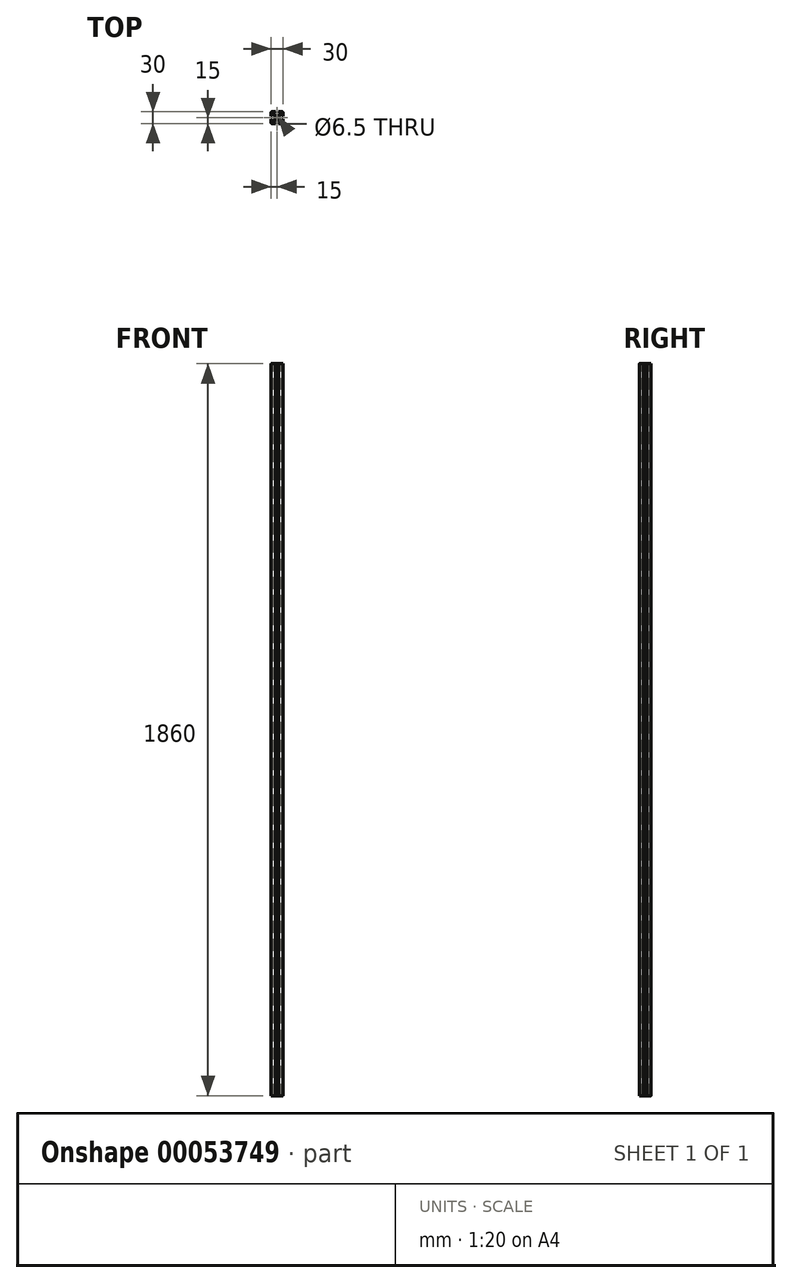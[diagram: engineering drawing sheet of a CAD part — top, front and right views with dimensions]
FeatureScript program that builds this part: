
annotation { "Feature Type Name" : "Feature", "Feature Type Description" : "" }
export const myFeature = defineFeature(function(context is Context, id is Id, definition is map)
    precondition{}
    {
        {
            var Q0;
            Q0=qCreatedBy(makeId("Top.planeOp"),FACE);
            var sketch = newSketch(context, id + "F0", { "sketchPlane" : qUnion([Q0])});
            skLineSegment(sketch, "E0.bottom", {"start": v(-15, 15) * mm, "end": v(15, 15) * mm});
            skLineSegment(sketch, "E0.top", {"start": v(-15, -15) * mm, "end": v(15, -15) * mm});
            skLineSegment(sketch, "E0.left", {"start": v(-15, 15) * mm, "end": v(-15, -15) * mm});
            skLineSegment(sketch, "E0.right", {"start": v(15, 15) * mm, "end": v(15, -15) * mm});
            skSolve(sketch);
        }
        {
            var Q0;
            Q0=qSketchRegion(id+"F0",true);
            extrude(context, id + "F1", {"entities" : qUnion([Q0]), "endBound" : BoundingType.SYMMETRIC, "depth" : (1900 - 40) * mm});
        }
        {
            var Q0;
            Q0=makeQuery(id+"F1.opExtrude","SWEPT_EDGE",EDGE,{"disambiguationData":[OSD([sQuery(id+"F0.wireOp",EDGE,"E0.bottom"),sQuery(id+"F0.wireOp",EDGE,"E0.right")])]});
            var Q1;
            Q1=makeQuery(id+"F1.opExtrude","SWEPT_EDGE",EDGE,{"disambiguationData":[OSD([sQuery(id+"F0.wireOp",EDGE,"E0.bottom"),sQuery(id+"F0.wireOp",EDGE,"E0.left")])]});
            var Q2;
            Q2=makeQuery(id+"F1.opExtrude","SWEPT_EDGE",EDGE,{"disambiguationData":[OSD([sQuery(id+"F0.wireOp",EDGE,"E0.top"),sQuery(id+"F0.wireOp",EDGE,"E0.right")])]});
            var Q3;
            Q3=makeQuery(id+"F1.opExtrude","SWEPT_EDGE",EDGE,{"disambiguationData":[OSD([sQuery(id+"F0.wireOp",EDGE,"E0.top"),sQuery(id+"F0.wireOp",EDGE,"E0.left")])]});
            fillet(context, id + "F2", {"entities" : qUnion([Q0, Q1, Q2, Q3]), "radius" : 2 * mm, "tangentPropagation" : true, "allowEdgeOverflow" : false});
        }
        {
            var Q0;
            Q0=makeQuery(id+"F1.opExtrude","CAP_FACE",FACE,{"disambiguationData":[OSD([sQuery(id+"F0.wireOp",EDGE,"E0.bottom"),sQuery(id+"F0.wireOp",EDGE,"E0.top"),sQuery(id+"F0.wireOp",EDGE,"E0.left"),sQuery(id+"F0.wireOp",EDGE,"E0.right")])],"isStart":false});
            var sketch = newSketch(context, id + "F3", { "sketchPlane" : qUnion([Q0])});
            skCircle(sketch, "E1", {"center": v(0, 0) * mm, "radius": 3.25 * mm});
            skSolve(sketch);
        }
        {
            var Q0;
            Q0=qSketchRegion(id+"F3",true);
            extrude(context, id + "F4", {"entities" : qUnion([Q0]), "operationType" : NewBodyOperationType.REMOVE, "endBound" : BoundingType.THROUGH_ALL, "oppositeDirection" : true, "depth" : 25 * mm});
        }
        {
            var Q0;
            Q0=makeQuery(id+"F1.opExtrude","CAP_FACE",FACE,{"disambiguationData":[OSD([sQuery(id+"F0.wireOp",EDGE,"E0.bottom"),sQuery(id+"F0.wireOp",EDGE,"E0.top"),sQuery(id+"F0.wireOp",EDGE,"E0.left"),sQuery(id+"F0.wireOp",EDGE,"E0.right")])],"isStart":false});
            var sketch = newSketch(context, id + "F5", { "sketchPlane" : qUnion([Q0])});
            skLineSegment(sketch, "E2", {"start": v(-4.2, 15) * mm, "end": v(4.2, 15) * mm});
            skLineSegment(sketch, "E3", {"start": v(4.2, 15) * mm, "end": v(4.2, 13) * mm});
            skLineSegment(sketch, "E4", {"start": v(4.2, 13) * mm, "end": v(8.25, 13) * mm});
            skLineSegment(sketch, "E5", {"start": v(8.25, 13) * mm, "end": v(8.25, 10) * mm});
            skLineSegment(sketch, "E6", {"start": v(8.25, 10) * mm, "end": v(3.85, 5.6) * mm});
            skLineSegment(sketch, "E7", {"start": v(3.85, 5.6) * mm, "end": v(-3.85, 5.6) * mm});
            skLineSegment(sketch, "E8", {"start": v(-3.85, 5.6) * mm, "end": v(-8.25, 10) * mm});
            skLineSegment(sketch, "E9", {"start": v(-4.2, 15) * mm, "end": v(-4.2, 13) * mm});
            skLineSegment(sketch, "E10", {"start": v(-4.2, 13) * mm, "end": v(-8.25, 13) * mm});
            skLineSegment(sketch, "E11", {"start": v(-8.25, 13) * mm, "end": v(-8.25, 10) * mm});
            skLineSegment(sketch, "E12.1.0", {"start": v(-15, -4.2) * mm, "end": v(-15, 4.2) * mm});
            skLineSegment(sketch, "E12.1.1", {"start": v(-15, 4.2) * mm, "end": v(-13, 4.2) * mm});
            skLineSegment(sketch, "E12.1.2", {"start": v(-13, 4.2) * mm, "end": v(-13, 8.25) * mm});
            skLineSegment(sketch, "E12.1.3", {"start": v(-13, 8.25) * mm, "end": v(-10, 8.25) * mm});
            skLineSegment(sketch, "E12.1.4", {"start": v(-10, 8.25) * mm, "end": v(-5.6, 3.85) * mm});
            skLineSegment(sketch, "E12.1.5", {"start": v(-5.6, 3.85) * mm, "end": v(-5.6, -3.85) * mm});
            skLineSegment(sketch, "E12.1.6", {"start": v(-5.6, -3.85) * mm, "end": v(-10, -8.25) * mm});
            skLineSegment(sketch, "E12.1.7", {"start": v(-13, -8.25) * mm, "end": v(-10, -8.25) * mm});
            skLineSegment(sketch, "E12.1.8", {"start": v(-13, -4.2) * mm, "end": v(-13, -8.25) * mm});
            skLineSegment(sketch, "E12.1.9", {"start": v(-15, -4.2) * mm, "end": v(-13, -4.2) * mm});
            skLineSegment(sketch, "E12.2.0", {"start": v(4.2, -15) * mm, "end": v(-4.2, -15) * mm});
            skLineSegment(sketch, "E12.2.1", {"start": v(-4.2, -15) * mm, "end": v(-4.2, -13) * mm});
            skLineSegment(sketch, "E12.2.2", {"start": v(-4.2, -13) * mm, "end": v(-8.25, -13) * mm});
            skLineSegment(sketch, "E12.2.3", {"start": v(-8.25, -13) * mm, "end": v(-8.25, -10) * mm});
            skLineSegment(sketch, "E12.2.4", {"start": v(-8.25, -10) * mm, "end": v(-3.85, -5.6) * mm});
            skLineSegment(sketch, "E12.2.5", {"start": v(-3.85, -5.6) * mm, "end": v(3.85, -5.6) * mm});
            skLineSegment(sketch, "E12.2.6", {"start": v(3.85, -5.6) * mm, "end": v(8.25, -10) * mm});
            skLineSegment(sketch, "E12.2.7", {"start": v(8.25, -13) * mm, "end": v(8.25, -10) * mm});
            skLineSegment(sketch, "E12.2.8", {"start": v(4.2, -13) * mm, "end": v(8.25, -13) * mm});
            skLineSegment(sketch, "E12.2.9", {"start": v(4.2, -15) * mm, "end": v(4.2, -13) * mm});
            skLineSegment(sketch, "E12.3.0", {"start": v(15, 4.2) * mm, "end": v(15, -4.2) * mm});
            skLineSegment(sketch, "E12.3.1", {"start": v(15, -4.2) * mm, "end": v(13, -4.2) * mm});
            skLineSegment(sketch, "E12.3.2", {"start": v(13, -4.2) * mm, "end": v(13, -8.25) * mm});
            skLineSegment(sketch, "E12.3.3", {"start": v(13, -8.25) * mm, "end": v(10, -8.25) * mm});
            skLineSegment(sketch, "E12.3.4", {"start": v(10, -8.25) * mm, "end": v(5.6, -3.85) * mm});
            skLineSegment(sketch, "E12.3.5", {"start": v(5.6, -3.85) * mm, "end": v(5.6, 3.85) * mm});
            skLineSegment(sketch, "E12.3.6", {"start": v(5.6, 3.85) * mm, "end": v(10, 8.25) * mm});
            skLineSegment(sketch, "E12.3.7", {"start": v(13, 8.25) * mm, "end": v(10, 8.25) * mm});
            skLineSegment(sketch, "E12.3.8", {"start": v(13, 4.2) * mm, "end": v(13, 8.25) * mm});
            skLineSegment(sketch, "E12.3.9", {"start": v(15, 4.2) * mm, "end": v(13, 4.2) * mm});
            skPoint(sketch, "E12.center", {"position": v(0, 0) * mm});
            skSolve(sketch);
        }
        {
            var Q0;
            Q0=qSketchRegion(id+"F5",true);
            extrude(context, id + "F6", {"entities" : qUnion([Q0]), "operationType" : NewBodyOperationType.REMOVE, "endBound" : BoundingType.THROUGH_ALL, "oppositeDirection" : true, "depth" : 25 * mm});
        }
    });
